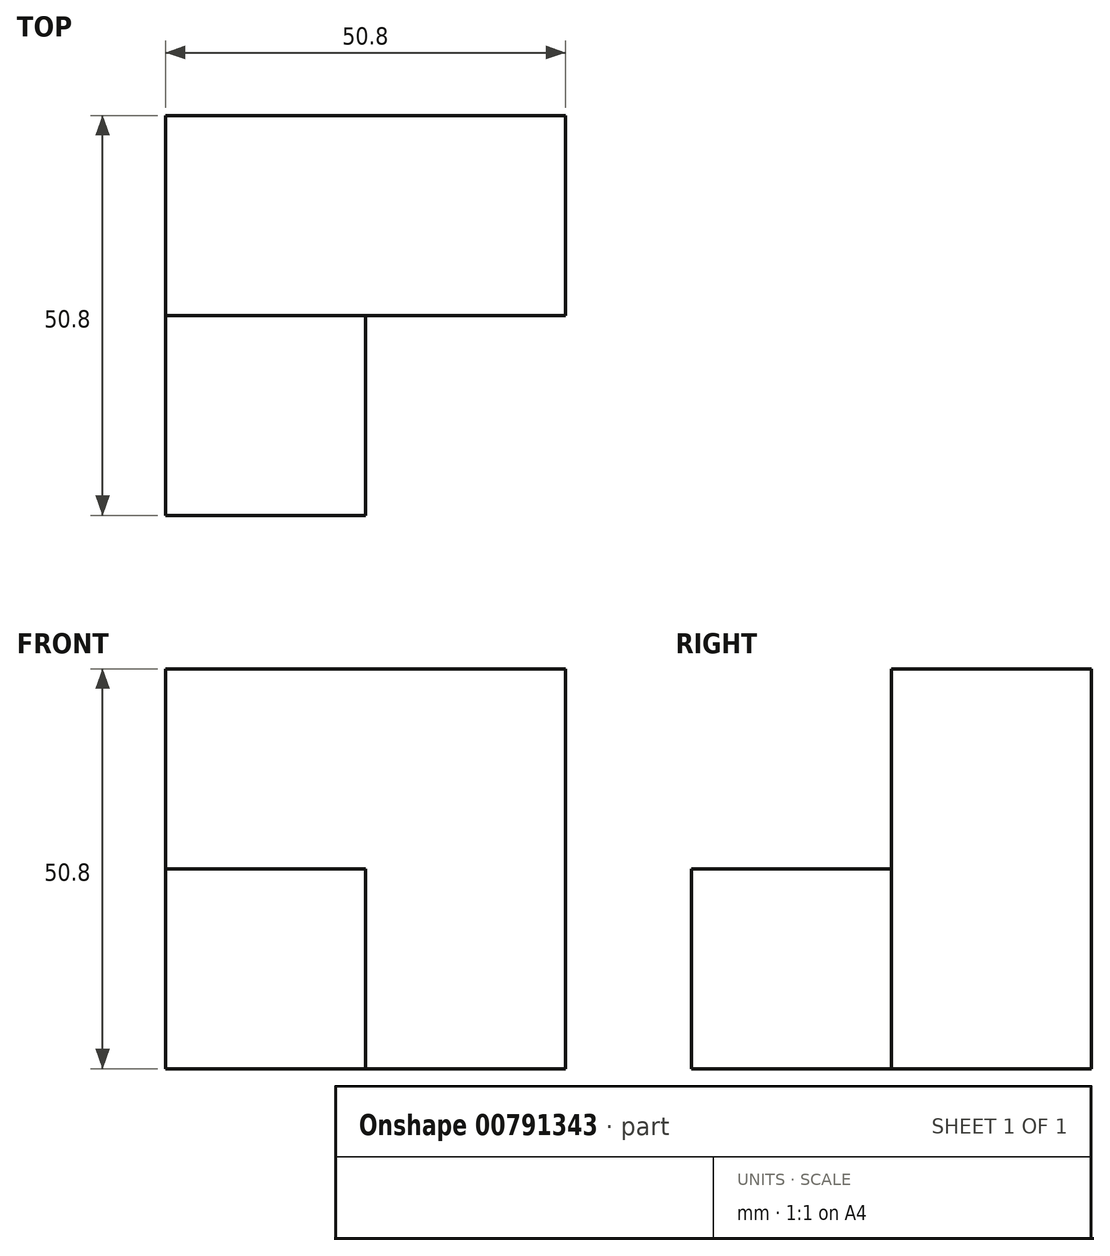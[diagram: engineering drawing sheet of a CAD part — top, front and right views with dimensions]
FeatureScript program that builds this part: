
annotation { "Feature Type Name" : "Feature", "Feature Type Description" : "" }
export const myFeature = defineFeature(function(context is Context, id is Id, definition is map)
    precondition{}
    {
        {
            var Q0;
            Q0=qCreatedBy(makeId("Front.planeOp"),FACE);
            var sketch = newSketch(context, id + "F0", { "sketchPlane" : qUnion([Q0])});
            skLineSegment(sketch, "E0", {"start": v(0, 50.8) * mm, "end": v(0, 0) * mm});
            skLineSegment(sketch, "E1", {"start": v(0, 0) * mm, "end": v(50.8, 0) * mm});
            skLineSegment(sketch, "E2", {"start": v(50.8, 0) * mm, "end": v(50.8, 50.8) * mm});
            skLineSegment(sketch, "E3", {"start": v(50.8, 50.8) * mm, "end": v(0, 50.8) * mm});
            skSolve(sketch);
        }
        {
            var Q0;
            Q0=qSketchRegion(id+"F0",true);
            extrude(context, id + "F1", {"entities" : qUnion([Q0]), "depth" : 25.4 * mm, "offsetDistance" : 25.4 * mm});
        }
        {
            var Q0;
            Q0=makeQuery(id+"F1.opExtrude","CAP_FACE",FACE,{"disambiguationData":[OSD([sQuery(id+"F0.wireOp",EDGE,"E0"),sQuery(id+"F0.wireOp",EDGE,"E1"),sQuery(id+"F0.wireOp",EDGE,"E2"),sQuery(id+"F0.wireOp",EDGE,"E3")])],"isStart":false});
            var sketch = newSketch(context, id + "F2", { "sketchPlane" : qUnion([Q0])});
            skLineSegment(sketch, "E4.bottom", {"start": v(0, 25.4) * mm, "end": v(25.4, 25.4) * mm});
            skLineSegment(sketch, "E4.top", {"start": v(0, 0) * mm, "end": v(25.4, 0) * mm});
            skLineSegment(sketch, "E4.left", {"start": v(0, 25.4) * mm, "end": v(0, 0) * mm});
            skLineSegment(sketch, "E4.right", {"start": v(25.4, 25.4) * mm, "end": v(25.4, 0) * mm});
            skSolve(sketch);
        }
        {
            var Q0;
            Q0=qSketchRegion(id+"F2",true);
            extrude(context, id + "F3", {"entities" : qUnion([Q0]), "operationType" : NewBodyOperationType.ADD, "depth" : 25.4 * mm, "offsetDistance" : 25.4 * mm});
        }
    });
